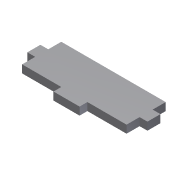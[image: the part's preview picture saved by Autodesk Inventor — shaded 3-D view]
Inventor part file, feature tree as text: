
AUTODESK INVENTOR PART (.ipt)
format: ipt  version: 2012 (Build 160160000, 160)  size: 88,576 bytes
history: native  units: mm
features: extrude x1, sketch x1
ambient origin geometry x8: Origin, YZ Plane, XZ Plane, XY Plane, X Axis, Y Axis, Z Axis, Center Point
bodies: Solid1 (feature_tree)
feature tree (2):
  extrude  "Extrusion1"  Depth=15.0mm
  sketch  "Sketch1"  dims[d3=3.0mm d5=15.0mm d6=3.0mm d7=10.0mm d8=3.0mm d9=15.0mm d10=3.0mm d11=0.0mm d14=5.0mm d15=15.0mm d16=5.0mm d17=5.0mm d18=5.0mm d19=3.0mm d20=3.0mm]
